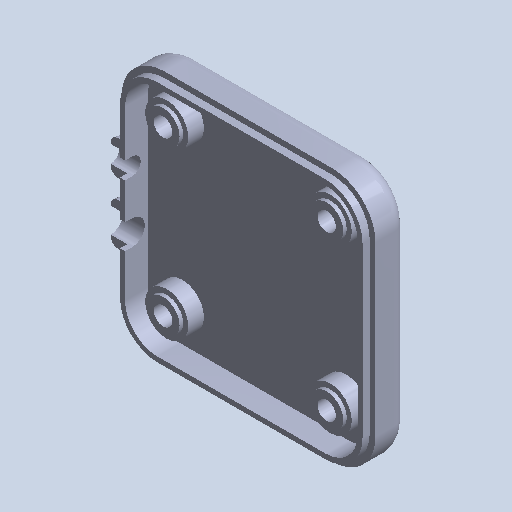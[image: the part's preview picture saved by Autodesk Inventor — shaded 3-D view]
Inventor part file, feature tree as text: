
AUTODESK INVENTOR PART (.ipt)
format: ipt  version: 2022.3 (Build 263350000, 350)  size: 210,944 bytes
history: native  units: mm (DEFAULTED — no unit token found)
features: fillet x1
ambient origin geometry x8: Origin, YZ Plane, XZ Plane, XY Plane, X Axis, Y Axis, Z Axis, Center Point
bodies: Solid1 (feature_tree)
feature tree (1):
  fillet  "Fillet5"  [1 undecoded]
note: 1 required parameter value undecoded (feature->parameter linkage not recoverable at this tier; creation-order binding heuristic only, values carry confidence <= 0.55)
